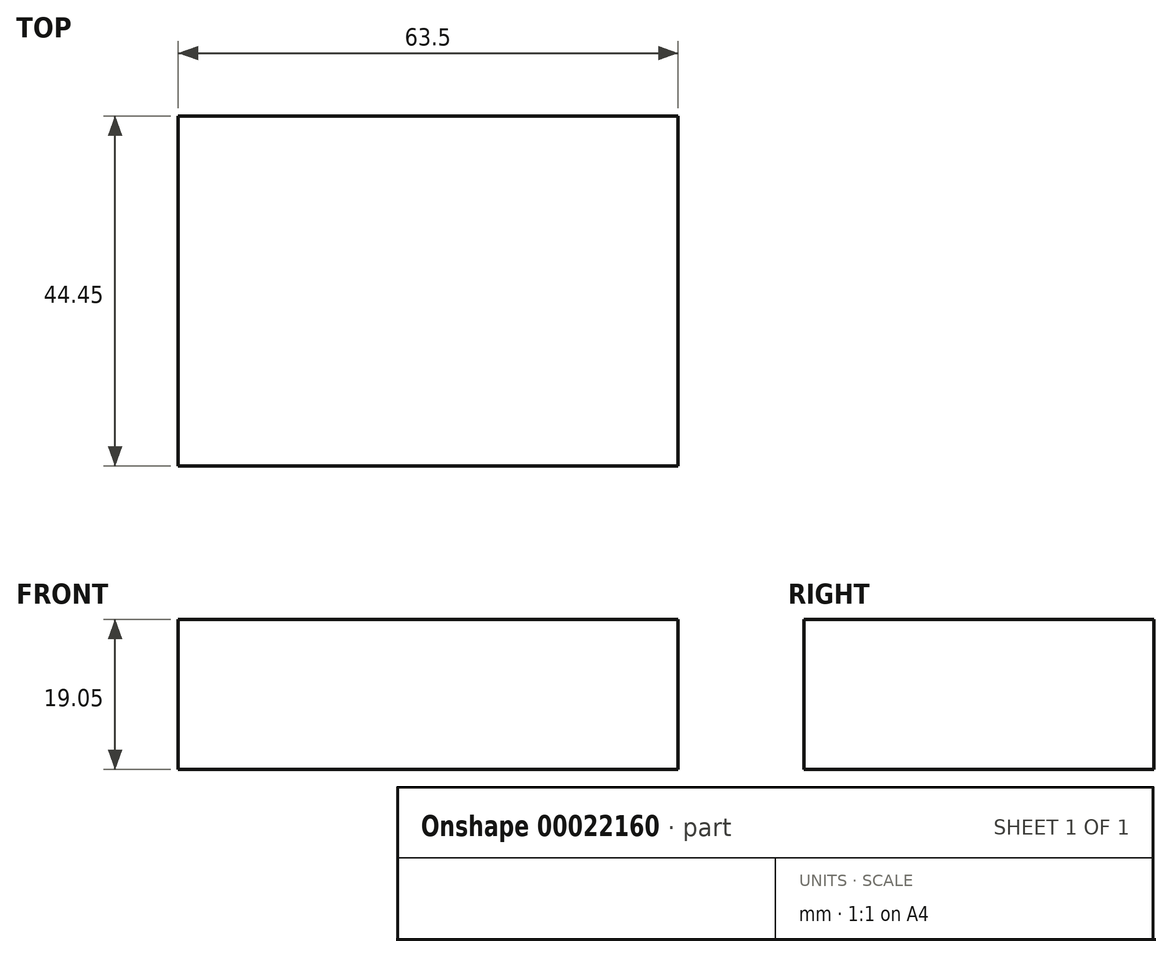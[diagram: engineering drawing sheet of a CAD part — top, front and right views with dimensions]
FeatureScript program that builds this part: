
annotation { "Feature Type Name" : "Feature", "Feature Type Description" : "" }
export const myFeature = defineFeature(function(context is Context, id is Id, definition is map)
    precondition{}
    {
        {
            var Q0;
            Q0=qCreatedBy(makeId("Top.planeOp"),FACE);
            var sketch = newSketch(context, id + "F0", { "sketchPlane" : qUnion([Q0])});
            skLineSegment(sketch, "E0.bottom", {"start": v(-10.02, 34.98) * mm, "end": v(53.48, 34.98) * mm});
            skLineSegment(sketch, "E0.top", {"start": v(-10.02, -9.47) * mm, "end": v(53.48, -9.47) * mm});
            skLineSegment(sketch, "E0.left", {"start": v(-10.02, 34.98) * mm, "end": v(-10.02, -9.47) * mm});
            skLineSegment(sketch, "E0.right", {"start": v(53.48, 34.98) * mm, "end": v(53.48, -9.47) * mm});
            skSolve(sketch);
        }
        {
            var Q0;
            Q0 = qSketchRegion(id + "F0", true);
            extrude(context, id + "F1", {"entities" : qUnion([Q0]), "depth" : 19.05 * mm});
        }
    });
